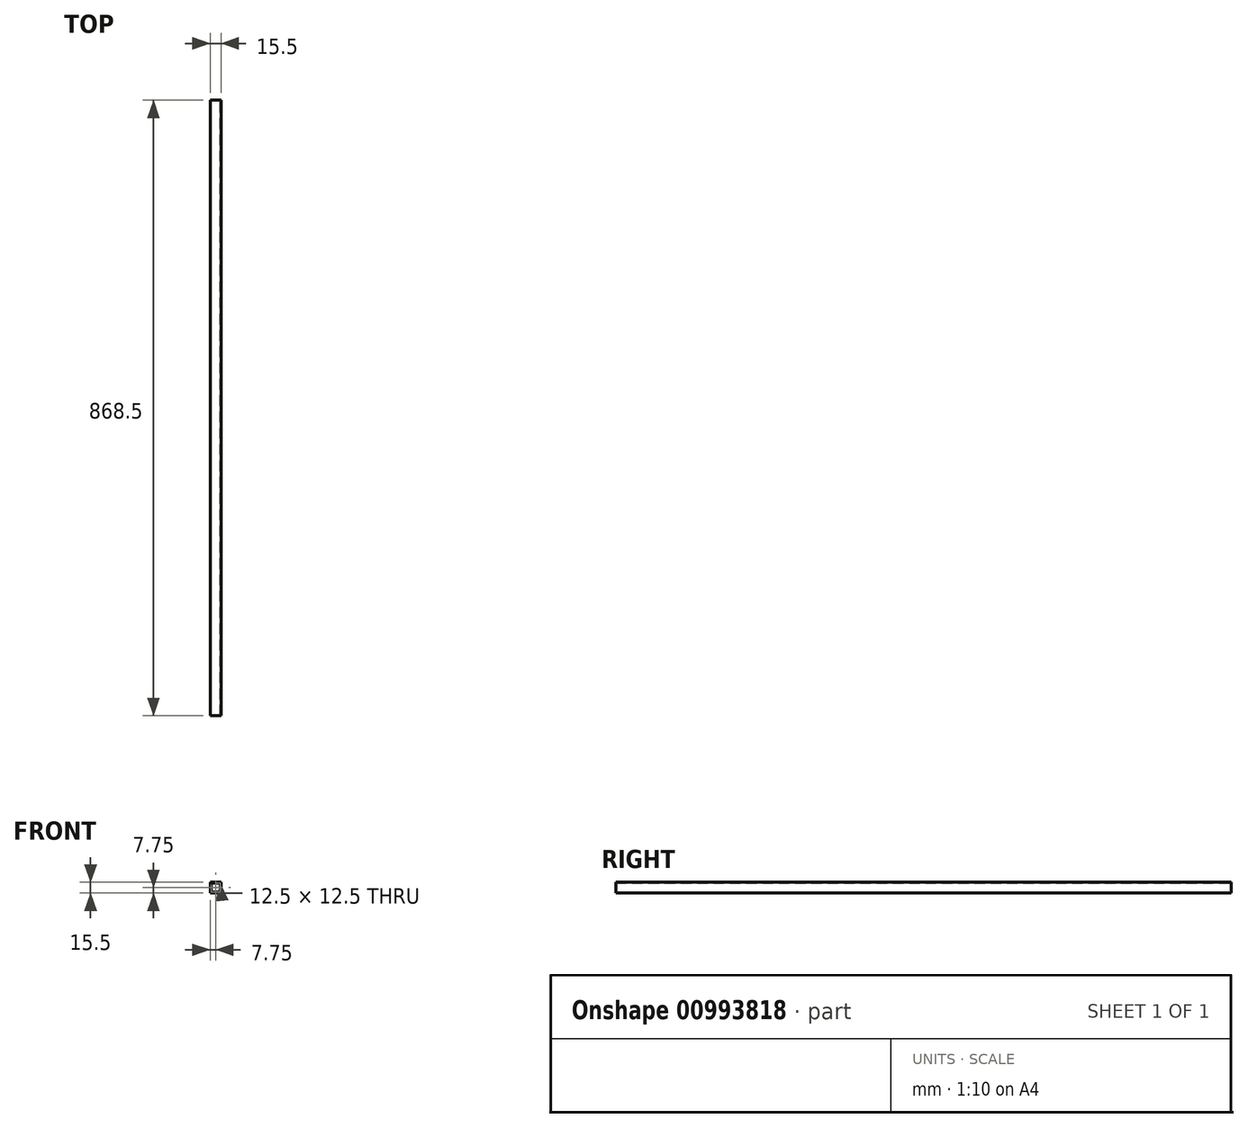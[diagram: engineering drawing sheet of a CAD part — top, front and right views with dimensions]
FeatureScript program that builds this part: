
annotation { "Feature Type Name" : "Feature", "Feature Type Description" : "" }
export const myFeature = defineFeature(function(context is Context, id is Id, definition is map)
    precondition{}
    {
        {
            var Q0;
            Q0=qCreatedBy(makeId("Front.planeOp"),FACE);
            var sketch = newSketch(context, id + "F0", { "sketchPlane" : qUnion([Q0])});
            skLineSegment(sketch, "E0.bottom", {"start": v(7.75, 7.75) * mm, "end": v(-7.75, 7.75) * mm});
            skLineSegment(sketch, "E0.top", {"start": v(7.75, -7.75) * mm, "end": v(-7.75, -7.75) * mm});
            skLineSegment(sketch, "E0.left", {"start": v(7.75, 7.75) * mm, "end": v(7.75, -7.75) * mm});
            skLineSegment(sketch, "E0.right", {"start": v(-7.75, 7.75) * mm, "end": v(-7.75, -7.75) * mm});
            skPoint(sketch, "E0.middle", {"position": v(0, 0) * mm});
            skLineSegment(sketch, "E1.bottom", {"start": v(6.25, 6.25) * mm, "end": v(-6.25, 6.25) * mm});
            skLineSegment(sketch, "E1.top", {"start": v(6.25, -6.25) * mm, "end": v(-6.25, -6.25) * mm});
            skLineSegment(sketch, "E1.left", {"start": v(6.25, 6.25) * mm, "end": v(6.25, -6.25) * mm});
            skLineSegment(sketch, "E1.right", {"start": v(-6.25, 6.25) * mm, "end": v(-6.25, -6.25) * mm});
            skSolve(sketch);
        }
        {
            var Q0;
            Q0=makeQuery(id+"F0.imprint","IMPRINT",FACE,{"disambiguationData":[TD([[makeQuery(id+"F0.imprint","IMPRINT",EDGE,{"derivedFrom":sQuery(id+"F0.wireOp",EDGE,"E0.bottom")}),1.0]])]});
            extrude(context, id + "F1", {"entities" : qUnion([Q0]), "depth" : 868.5 * mm, "offsetDistance" : 25 * mm, "symmetric" : true});
        }
    });
